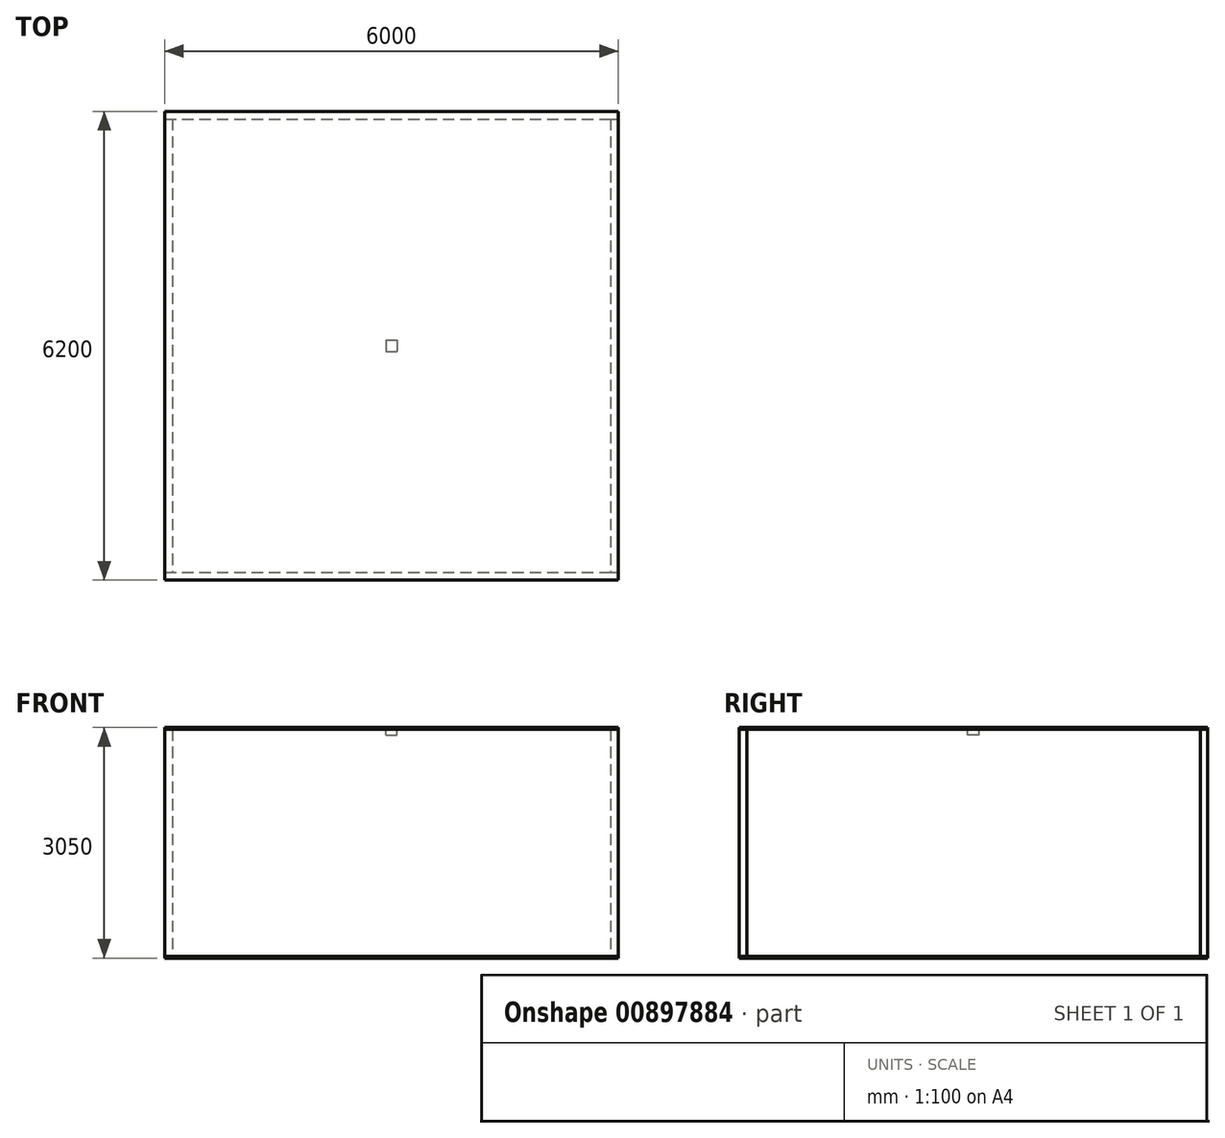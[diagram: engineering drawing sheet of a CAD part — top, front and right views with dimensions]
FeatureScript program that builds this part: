
annotation { "Feature Type Name" : "Feature", "Feature Type Description" : "" }
export const myFeature = defineFeature(function(context is Context, id is Id, definition is map)
    precondition{}
    {
        {
            var Q0;
            Q0=qCreatedBy(makeId("Top.planeOp"),FACE);
            var sketch = newSketch(context, id + "F0", { "sketchPlane" : qUnion([Q0])});
            skLineSegment(sketch, "E0.bottom", {"start": v(-3000, 3000) * mm, "end": v(3000, 3000) * mm});
            skLineSegment(sketch, "E0.top", {"start": v(-3000, -3000) * mm, "end": v(3000, -3000) * mm});
            skLineSegment(sketch, "E0.left", {"start": v(-2900, 3000) * mm, "end": v(-2900, -3000) * mm});
            skLineSegment(sketch, "E0.right", {"start": v(2900, 3000) * mm, "end": v(2900, -3000) * mm});
            skPoint(sketch, "E0.middle", {"position": v(0, 0) * mm});
            skLineSegment(sketch, "E1.0", {"start": v(-3000, 3100) * mm, "end": v(3000, 3100) * mm});
            skLineSegment(sketch, "E1.1", {"start": v(-3000, 3100) * mm, "end": v(-3000, -3100) * mm});
            skLineSegment(sketch, "E1.2", {"start": v(-3000, -3100) * mm, "end": v(3000, -3100) * mm});
            skLineSegment(sketch, "E1.3", {"start": v(3000, 3100) * mm, "end": v(3000, -3100) * mm});
            skSolve(sketch);
        }
        {
            var Q0;
            {var subQ0=sQuery(id+"F0.wireOp",EDGE,"E1.0");Q0=makeQuery(id+"F0.imprint","IMPRINT",FACE,{"disambiguationData":[TD([[makeQuery(id+"F0.imprint","IMPRINT",EDGE,{"derivedFrom":subQ0}),-1.0]])]});}
            extrude(context, id + "F1", {"entities" : qUnion([Q0]), "depth" : 3000 * mm, "offsetDistance" : 25 * mm});
        }
        {
            var Q0;
            {var subQ3=sQuery(id+"F0.wireOp",EDGE,"E0.left");Q0=makeQuery(id+"F0.imprint","IMPRINT",FACE,{"disambiguationData":[TD([[makeQuery(id+"F0.imprint","IMPRINT",EDGE,{"derivedFrom":subQ3}),-1.0]])]});}
            var Q1;
            Q1=makeQuery(id+"F1.opExtrude","CAP_VERTEX",VERTEX,{"disambiguationData":[OSD([sQuery(id+"F0.wireOp",EDGE,"E0.bottom"),sQuery(id+"F0.wireOp",EDGE,"E1.1")])],"isStart":false});
            extrude(context, id + "F2", {"entities" : qUnion([Q0]), "endBound" : BoundingType.UP_TO_VERTEX, "depth" : 25 * mm, "endBoundEntityVertex" : qUnion([Q1]), "offsetDistance" : 25 * mm});
        }
        {
            var Q0;
            {var subQ3=sQuery(id+"F0.wireOp",EDGE,"E1.2");Q0=makeQuery(id+"F0.imprint","IMPRINT",FACE,{"disambiguationData":[TD([[makeQuery(id+"F0.imprint","IMPRINT",EDGE,{"derivedFrom":subQ3}),1.0]])]});}
            var Q1;
            Q1=makeQuery(id+"F1.opExtrude","CAP_VERTEX",VERTEX,{"disambiguationData":[OSD([sQuery(id+"F0.wireOp",EDGE,"E0.bottom"),sQuery(id+"F0.wireOp",EDGE,"E1.3")])],"isStart":false});
            extrude(context, id + "F3", {"entities" : qUnion([Q0]), "endBound" : BoundingType.UP_TO_VERTEX, "depth" : 25 * mm, "endBoundEntityVertex" : qUnion([Q1]), "offsetDistance" : 25 * mm});
        }
        {
            var Q0;
            {var subQ3=sQuery(id+"F0.wireOp",EDGE,"E0.right");Q0=makeQuery(id+"F0.imprint","IMPRINT",FACE,{"disambiguationData":[TD([[makeQuery(id+"F0.imprint","IMPRINT",EDGE,{"derivedFrom":subQ3}),1.0]])]});}
            var Q1;
            Q1=makeQuery(id+"F1.opExtrude","CAP_VERTEX",VERTEX,{"disambiguationData":[OSD([sQuery(id+"F0.wireOp",EDGE,"E0.bottom"),sQuery(id+"F0.wireOp",EDGE,"E1.3")])],"isStart":false});
            extrude(context, id + "F4", {"entities" : qUnion([Q0]), "endBound" : BoundingType.UP_TO_VERTEX, "depth" : 25 * mm, "endBoundEntityVertex" : qUnion([Q1]), "offsetDistance" : 25 * mm});
        }
        {
            var Q0;
            {var subQ3=sQuery(id+"F0.wireOp",EDGE,"E1.2");Q0=makeQuery(id+"F0.imprint","IMPRINT",FACE,{"disambiguationData":[TD([[makeQuery(id+"F0.imprint","IMPRINT",EDGE,{"derivedFrom":subQ3}),1.0]])]});}
            var Q1;
            {var subQ3=sQuery(id+"F0.wireOp",EDGE,"E0.left");Q1=makeQuery(id+"F0.imprint","IMPRINT",FACE,{"disambiguationData":[TD([[makeQuery(id+"F0.imprint","IMPRINT",EDGE,{"derivedFrom":subQ3}),-1.0]])]});}
            var Q2;
            {var subQ0=sQuery(id+"F0.wireOp",EDGE,"E0.left");Q2=makeQuery(id+"F0.imprint","IMPRINT",FACE,{"disambiguationData":[TD([[makeQuery(id+"F0.imprint","IMPRINT",EDGE,{"derivedFrom":subQ0}),1.0]])]});}
            var Q3;
            {var subQ0=sQuery(id+"F0.wireOp",EDGE,"E1.0");Q3=makeQuery(id+"F0.imprint","IMPRINT",FACE,{"disambiguationData":[TD([[makeQuery(id+"F0.imprint","IMPRINT",EDGE,{"derivedFrom":subQ0}),-1.0]])]});}
            var Q4;
            {var subQ3=sQuery(id+"F0.wireOp",EDGE,"E0.right");Q4=makeQuery(id+"F0.imprint","IMPRINT",FACE,{"disambiguationData":[TD([[makeQuery(id+"F0.imprint","IMPRINT",EDGE,{"derivedFrom":subQ3}),1.0]])]});}
            extrude(context, id + "F5", {"entities" : qUnion([Q0, Q1, Q2, Q3, Q4]), "oppositeDirection" : true, "depth" : 25 * mm, "offsetDistance" : 25 * mm});
        }
        {
            var Q0;
            Q0=makeQuery(id+"F1.opExtrude","CAP_FACE",FACE,{"disambiguationData":[OSD([sQuery(id+"F0.wireOp",EDGE,"E0.bottom"),sQuery(id+"F0.wireOp",EDGE,"E1.0"),sQuery(id+"F0.wireOp",EDGE,"E1.1"),sQuery(id+"F0.wireOp",EDGE,"E1.3")])],"isStart":false});
            var sketch = newSketch(context, id + "F6", { "sketchPlane" : qUnion([Q0])});
            skLineSegment(sketch, "E2.bottom", {"start": v(-3000, 3100) * mm, "end": v(3000, 3100) * mm});
            skLineSegment(sketch, "E2.top", {"start": v(-3000, -3100) * mm, "end": v(3000, -3100) * mm});
            skLineSegment(sketch, "E2.left", {"start": v(-3000, 3100) * mm, "end": v(-3000, -3100) * mm});
            skLineSegment(sketch, "E2.right", {"start": v(3000, 3100) * mm, "end": v(3000, -3100) * mm});
            skLineSegment(sketch, "E3.bottom", {"start": v(-75, 75) * mm, "end": v(75, 75) * mm});
            skLineSegment(sketch, "E3.top", {"start": v(-75, -75) * mm, "end": v(75, -75) * mm});
            skLineSegment(sketch, "E3.left", {"start": v(-75, 75) * mm, "end": v(-75, -75) * mm});
            skLineSegment(sketch, "E3.right", {"start": v(75, 75) * mm, "end": v(75, -75) * mm});
            skPoint(sketch, "E3.middle", {"position": v(0, 0) * mm});
            skSolve(sketch);
        }
        {
            var Q0;
            Q0 = qSketchRegion(id + "F6", true);
            var Q1;
            Q1=makeQuery(id+"F6.imprint","IMPRINT",FACE,{"disambiguationData":[TD([[makeQuery(id+"F6.imprint","IMPRINT",EDGE,{"derivedFrom":sQuery(id+"F6.wireOp",EDGE,"E3.bottom")}),-1.0]])]});
            extrude(context, id + "F7", {"entities" : qUnion([Q0, Q1]), "depth" : 25 * mm, "offsetDistance" : 25 * mm});
        }
        {
            var Q0;
            Q0=makeQuery(id+"F6.imprint","IMPRINT",FACE,{"disambiguationData":[TD([[makeQuery(id+"F6.imprint","IMPRINT",EDGE,{"derivedFrom":sQuery(id+"F6.wireOp",EDGE,"E3.bottom")}),-1.0]])]});
            extrude(context, id + "F8", {"entities" : qUnion([Q0]), "oppositeDirection" : true, "depth" : 75 * mm, "offsetDistance" : 25 * mm});
        }
    });
